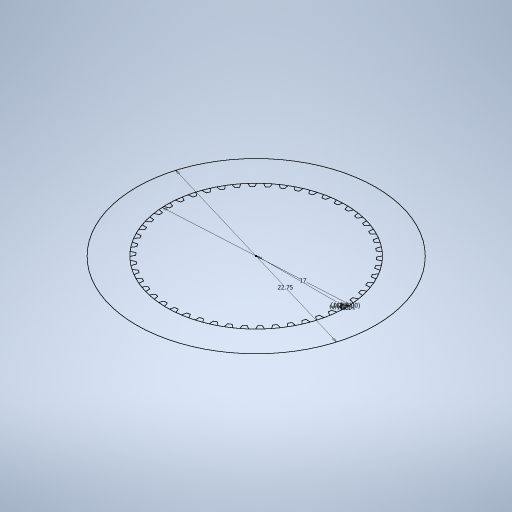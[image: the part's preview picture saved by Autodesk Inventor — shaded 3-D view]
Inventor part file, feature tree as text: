
AUTODESK INVENTOR PART (.ipt)
format: ipt  version: 2023 (Build 270158000, 158)  size: 300,032 bytes
history: native  units: in
note: dims shown in document units (in); Inventor stores cm internally (conversion verified against a paired STEP export)
features: sketch x1
ambient origin geometry x8: Origin, YZ Plane, XZ Plane, XY Plane, X Axis, Y Axis, Z Axis, Center Point
feature tree (1):
  sketch  "Sketch1"  dims[d0=8.9567in d1=6.6929in d2=0.1181in d3=3.189in d4=0.2362in d5=0.7614in d6=0.7614in d7=19.685in d9=360.0deg]
